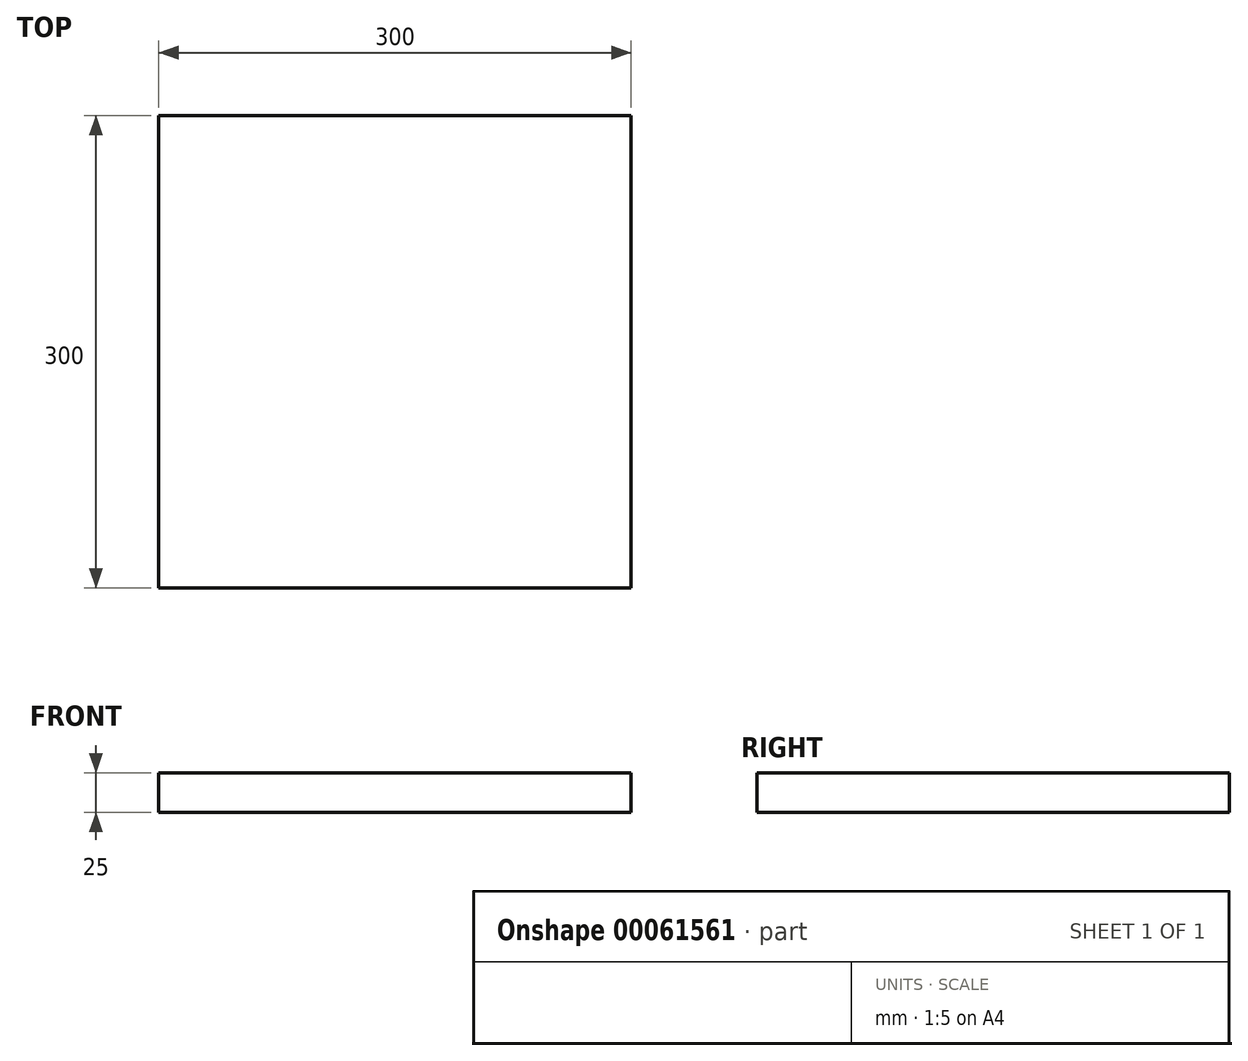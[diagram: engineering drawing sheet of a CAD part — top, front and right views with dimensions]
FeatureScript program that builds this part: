
annotation { "Feature Type Name" : "Feature", "Feature Type Description" : "" }
export const myFeature = defineFeature(function(context is Context, id is Id, definition is map)
    precondition{}
    {
        {
            var Q0;
            Q0=qCreatedBy(makeId("Top.planeOp"),FACE);
            var sketch = newSketch(context, id + "F0", { "sketchPlane" : qUnion([Q0])});
            skLineSegment(sketch, "E0.bottom", {"start": v(150, 150) * mm, "end": v(-150, 150) * mm});
            skLineSegment(sketch, "E0.top", {"start": v(150, -150) * mm, "end": v(-150, -150) * mm});
            skLineSegment(sketch, "E0.left", {"start": v(150, 150) * mm, "end": v(150, -150) * mm});
            skLineSegment(sketch, "E0.right", {"start": v(-150, 150) * mm, "end": v(-150, -150) * mm});
            skPoint(sketch, "E0.middle", {"position": v(0, 0) * mm});
            skSolve(sketch);
        }
        {
            var Q0;
            Q0=makeQuery(id+"F0.imprint","IMPRINT",FACE,{"disambiguationData":[TD([[makeQuery(id+"F0.imprint","IMPRINT",EDGE,{"derivedFrom":sQuery(id+"F0.wireOp",EDGE,"E0.bottom")}),1.0]])]});
            extrude(context, id + "F1", {"entities" : qUnion([Q0]), "depth" : 25 * mm, "offsetDistance" : 25 * mm});
        }
    });
